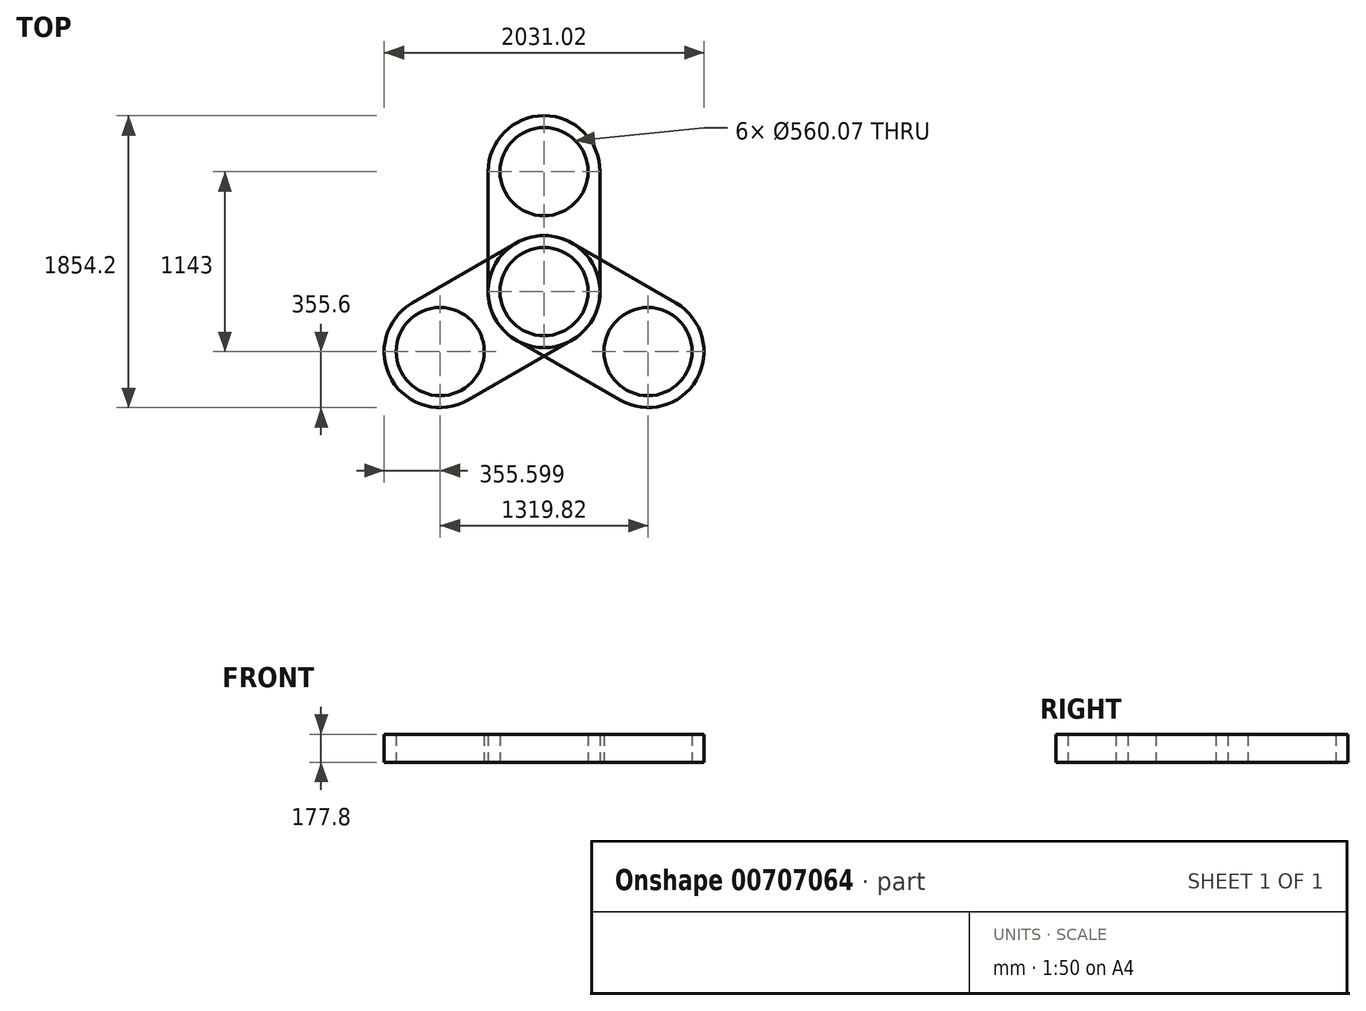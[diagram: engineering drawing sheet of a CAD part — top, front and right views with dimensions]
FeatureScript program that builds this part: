
annotation { "Feature Type Name" : "Feature", "Feature Type Description" : "" }
export const myFeature = defineFeature(function(context is Context, id is Id, definition is map)
    precondition{}
    {
        {
            var Q0;
            Q0=qCreatedBy(makeId("Top.planeOp"),FACE);
            var sketch = newSketch(context, id + "F0", { "sketchPlane" : qUnion([Q0])});
            skLineSegment(sketch, "E0.bottom", {"start": v(0, 0) * mm, "end": v(711.2, 0) * mm});
            skLineSegment(sketch, "E0.top", {"start": v(0, -762) * mm, "end": v(711.2, -762) * mm});
            skLineSegment(sketch, "E0.left", {"start": v(0, 0) * mm, "end": v(0, -762) * mm});
            skLineSegment(sketch, "E0.right", {"start": v(711.2, 0) * mm, "end": v(711.2, -762) * mm});
            skCircle(sketch, "E1", {"center": v(355.6, 0) * mm, "radius": 355.6 * mm});
            skCircle(sketch, "E2", {"center": v(355.6, 0) * mm, "radius": 280.04 * mm});
            skCircle(sketch, "E3", {"center": v(355.6, -762) * mm, "radius": 355.6 * mm});
            skCircle(sketch, "E4", {"center": v(355.6, -762) * mm, "radius": 280.04 * mm});
            skSolve(sketch);
        }
        {
            var Q0;
            Q0 = qSketchRegion(id + "F0", true);
            extrude(context, id + "F1", {"entities" : qUnion([Q0]), "depth" : 177.8 * mm, "offsetDistance" : 25.4 * mm});
        }
        {
            var Q0;
            Q0=makeQuery(id+"F1.opExtrude","SWEPT_BODY",BODY,{"disambiguationData":[OSD([sQuery(id+"F0.wireOp",EDGE,"E0.left"),sQuery(id+"F0.wireOp",EDGE,"E0.right"),sQuery(id+"F0.wireOp",EDGE,"E1"),sQuery(id+"F0.wireOp",EDGE,"E2"),sQuery(id+"F0.wireOp",EDGE,"E3"),sQuery(id+"F0.wireOp",EDGE,"E4")])]});
            var Q1;
            Q1=makeQuery(id+"F1.opExtrude","SWEPT_FACE",FACE,{"disambiguationData":[OSD([sQuery(id+"F0.wireOp",EDGE,"E3")])]});
            circularPattern(context, id + "F2", {"entities" : qUnion([Q0]), "axis" : qUnion([Q1]), "angle" : 360 * degree, "instanceCount" : 3, "equalSpace" : true});
        }
    });
